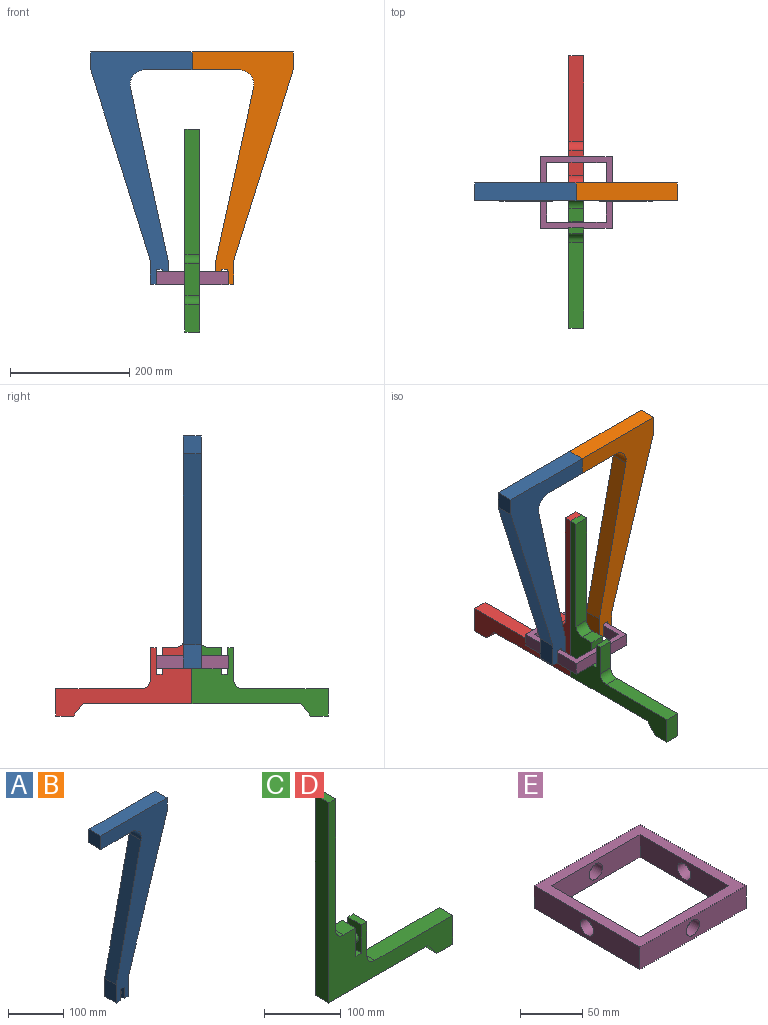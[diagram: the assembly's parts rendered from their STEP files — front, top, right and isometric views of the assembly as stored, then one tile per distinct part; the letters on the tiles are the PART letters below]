
ASSEMBLY  parts=5 mates=5
PART A: 17 faces, bbox 170x30x390 mm
  f0: plane 40x30mm, normal (1,0,0), area 1200mm2, adj f1,f13,f14,f15
  f1: plane 320x100mm, normal (0.95,0,-0.3), area 10057.8mm2, adj f0,f2,f14,f15
  f2: plane 30x30mm, normal (1,0,0), area 900mm2, adj f1,f3,f14,f15
  f3: plane 170x30mm, normal (0,0,1), area 5100mm2, adj f2,f4,f14,f15
  f4: plane 30x30mm, normal (-1,0,0), area 900mm2, adj f3,f5,f14,f15
  f5: plane 78.94x30mm, normal (0,0,-1), area 2368.2mm2, adj f4,f6,f14,f15
  f6: cylinder r=25mm len=30.34mm, axis (0,1,0), area 1339.6mm2, adj f5,f7,f14,f15
  f7: plane 289.66x63.36mm, normal (-0.98,0,0.21), area 8895.2mm2, adj f6,f8,f14,f15
  f8: plane 40x30mm, normal (-1,0,0), area 1200mm2, adj f7,f9,f14,f15
  f9: plane 30x10mm, normal (0,0,-1), area 300mm2, adj f8,f10,f14,f15
  f10: plane 30x25mm, normal (1,0,0), area 573.3mm2, adj f9,f11,f14,f15,f16
  f11: plane 30x10mm, normal (0,0,-1), area 300mm2, adj f10,f12,f14,f15
  f12: plane 30x25mm, normal (-1,0,0), area 573.3mm2, adj f11,f13,f14,f15,f16
  f13: plane 30x10mm, normal (0,0,-1), area 300mm2, adj f0,f12,f14,f15
  f14: plane 390x170mm, normal (0,-1,0), area 20668.3mm2, adj f0,f1,f2,f3,f4,f5,f6,f7
  f15: plane 390x170mm, normal (0,1,0), area 20668.3mm2, adj f0,f1,f2,f3,f4,f5,f6,f7
  f16: cylinder r=7.5mm len=15mm, axis (1,0,0), area 471.2mm2, adj f10,f12
PART B: same geometry as A
PART C: 19 faces, bbox 228.5x25x340 mm
  f0: plane 54.06x25mm, normal (1,0,0), area 1351.5mm2, adj f1,f15,f16,f17
  f1: plane 25x10mm, normal (0,0,1), area 250mm2, adj f0,f2,f16,f17
  f2: plane 45x25mm, normal (-1,0,0), area 948.3mm2, adj f1,f3,f16,f17,f18
  f3: plane 25x10mm, normal (0,0,1), area 250mm2, adj f2,f4,f16,f17
  f4: plane 45x25mm, normal (1,0,0), area 948.3mm2, adj f3,f5,f16,f17,f18
  f5: plane 25x22.5mm, normal (0,0,1), area 562.5mm2, adj f4,f6,f16,f17
  f6: cylinder r=15mm len=25mm, axis (0,1,0), area 589mm2, adj f5,f7,f16,f17
  f7: plane 210x25mm, normal (1,0,0), area 5250mm2, adj f6,f8,f16,f17
  f8: plane 25x12.5mm, normal (0,0,1), area 312.5mm2, adj f7,f9,f16,f17
  f9: plane 319.63x25mm, normal (-1,0,0), area 7990.8mm2, adj f8,f10,f16,f17
  f10: plane 182.61x25mm, normal (0,0,-1), area 4565.2mm2, adj f9,f11,f16,f17
  f11: plane 25x20.37mm, normal (-0.78,0,-0.63), area 656.4mm2, adj f10,f12,f16,f17
  f12: plane 29.29x25mm, normal (0,0,-1), area 732.1mm2, adj f11,f13,f16,f17
  f13: plane 45.94x25mm, normal (1,0,0), area 1148.5mm2, adj f12,f14,f16,f17
  f14: plane 143.46x25mm, normal (0,0,1), area 3586.5mm2, adj f13,f15,f16,f17
  f15: cylinder r=15mm len=25mm, axis (0,1,0), area 589mm2, adj f0,f14,f16,f17
  f16: plane 340x228.46mm, normal (0,-1,0), area 13900.7mm2, adj f0,f1,f2,f3,f4,f5,f6,f7
  f17: plane 340x228.46mm, normal (0,1,0), area 13900.7mm2, adj f0,f1,f2,f3,f4,f5,f6,f7
  f18: cylinder r=7.5mm len=15mm, axis (1,0,0), area 471.2mm2, adj f2,f4
PART D: same geometry as C
PART E: 14 faces, bbox 120x120x22 mm
  f0: plane 120x22mm, normal (-1,0,0), area 2463.3mm2, adj f1,f7,f8,f9,f13
  f1: plane 120x22mm, normal (0,-1,0), area 2463.3mm2, adj f0,f2,f8,f9,f11
  f2: plane 120x22mm, normal (1,0,0), area 2463.3mm2, adj f1,f7,f8,f9,f12
  f3: plane 100x22mm, normal (0,1,0), area 2023.3mm2, adj f4,f6,f8,f9,f11
  f4: plane 100x22mm, normal (1,0,0), area 2023.3mm2, adj f3,f5,f8,f9,f13
  f5: plane 100x22mm, normal (0,-1,0), area 2023.3mm2, adj f4,f6,f8,f9,f10
  f6: plane 100x22mm, normal (-1,0,0), area 2023.3mm2, adj f3,f5,f8,f9,f12
  f7: plane 120x22mm, normal (0,1,0), area 2463.3mm2, adj f0,f2,f8,f9,f10
  f8: plane 120x120mm, normal (0,0,1), area 4400mm2, adj f0,f1,f2,f3,f4,f5,f6,f7
  f9: plane 120x120mm, normal (0,0,-1), area 4400mm2, adj f0,f1,f2,f3,f4,f5,f6,f7
  f10: cylinder r=7.5mm len=15mm, axis (0,-1,0), area 471.2mm2, adj f5,f7
  f11: cylinder r=7.5mm len=15mm, axis (0,-1,0), area 471.2mm2, adj f1,f3
  f12: cylinder r=7.5mm len=15mm, axis (-1,0,0), area 471.2mm2, adj f2,f6
  f13: cylinder r=7.5mm len=15mm, axis (-1,0,0), area 471.2mm2, adj f0,f4
PLACE A rot(axis=(0,0,1),180deg) t=(107.68,143.98,-28.16)mm
PLACE B t=(107.68,173.98,-28.16)mm
PLACE C rot(axis=(0,0,-1),90deg) t=(120.68,159.58,-118.16)mm
PLACE D rot(axis=(0,0,1),90deg) t=(95.68,159.58,-118.16)mm
PLACE E t=(51.68,109.25,-39.16)mm
MATE cylindrical E.f12 <-> B.f16  axis (-1,0,0) through (163.18,158.98,-28.16)mm
MATE planar C.f9 <-> D.f9  axis (0,1,0) through (108.18,159.58,62.03)mm
MATE fastened C.f9 <-> D.f9  axis (0,1,0) through (108.18,159.58,62.03)mm
MATE fastened A.f4 <-> B.f4  axis (1,0,0) through (107.68,158.98,336.84)mm
MATE cylindrical D.f18 <-> E.f10  axis (0,1,0) through (108.18,214.58,-28.16)mm
